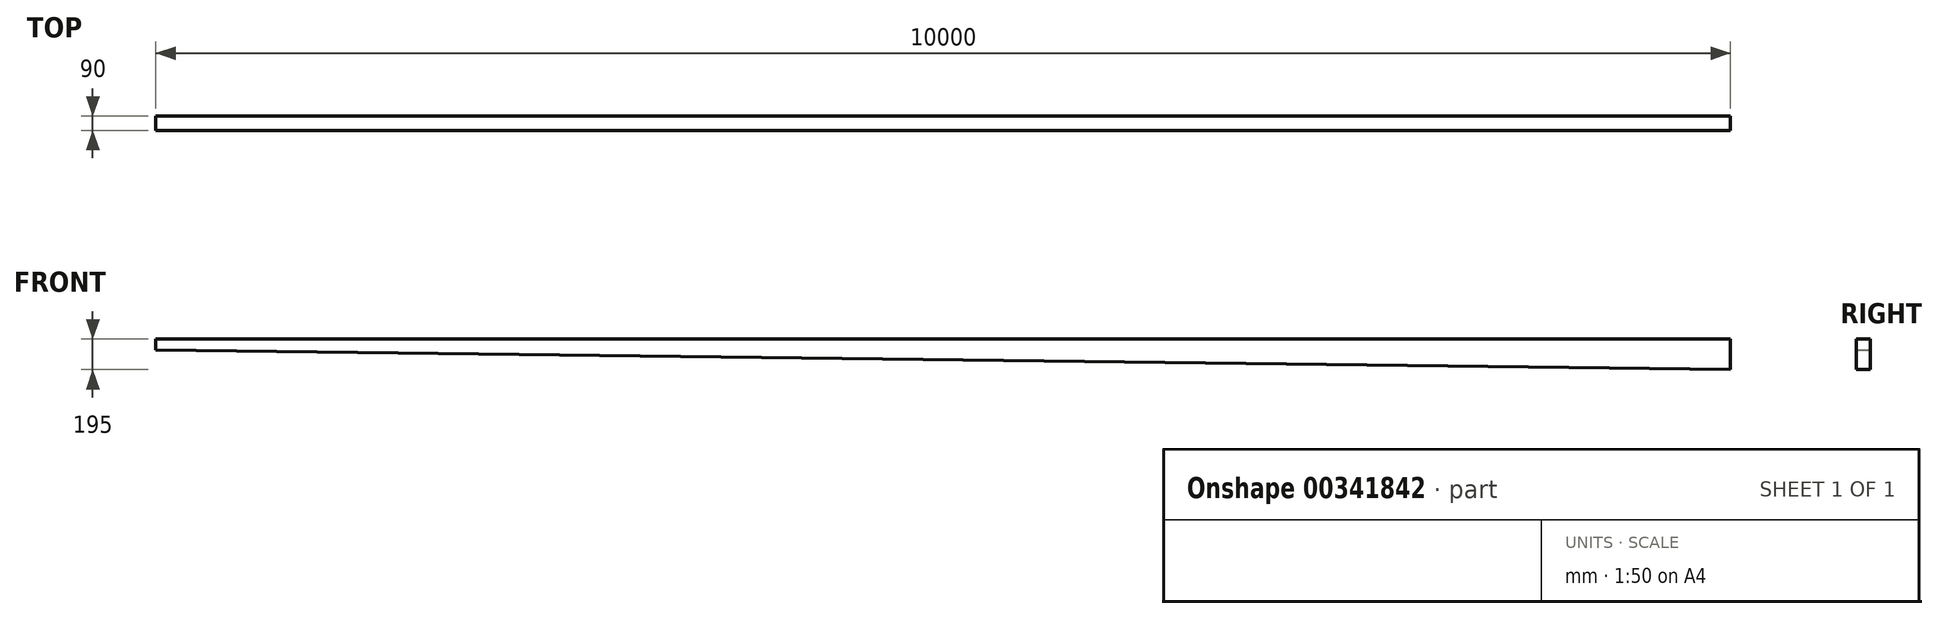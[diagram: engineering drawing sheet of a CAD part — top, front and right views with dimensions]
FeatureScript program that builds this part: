
annotation { "Feature Type Name" : "Feature", "Feature Type Description" : "" }
export const myFeature = defineFeature(function(context is Context, id is Id, definition is map)
    precondition{}
    {
        {
            var Q0;
            Q0=qCreatedBy(makeId("Front.planeOp"),FACE);
            var sketch = newSketch(context, id + "F0", { "sketchPlane" : qUnion([Q0])});
            skLineSegment(sketch, "E0", {"start": v(0, 0) * mm, "end": v(0, 70) * mm});
            skLineSegment(sketch, "E1", {"start": v(0, 70) * mm, "end": v(10000, 70) * mm});
            skLineSegment(sketch, "E2", {"start": v(10000, 70) * mm, "end": v(10000, -125) * mm});
            skLineSegment(sketch, "E3", {"start": v(10000, -125) * mm, "end": v(0, 0) * mm});
            skSolve(sketch);
        }
        {
            var Q0;
            Q0 = qSketchRegion(id + "F0", true);
            extrude(context, id + "F1", {"entities" : qUnion([Q0]), "depth" : 90 * mm});
        }
    });
